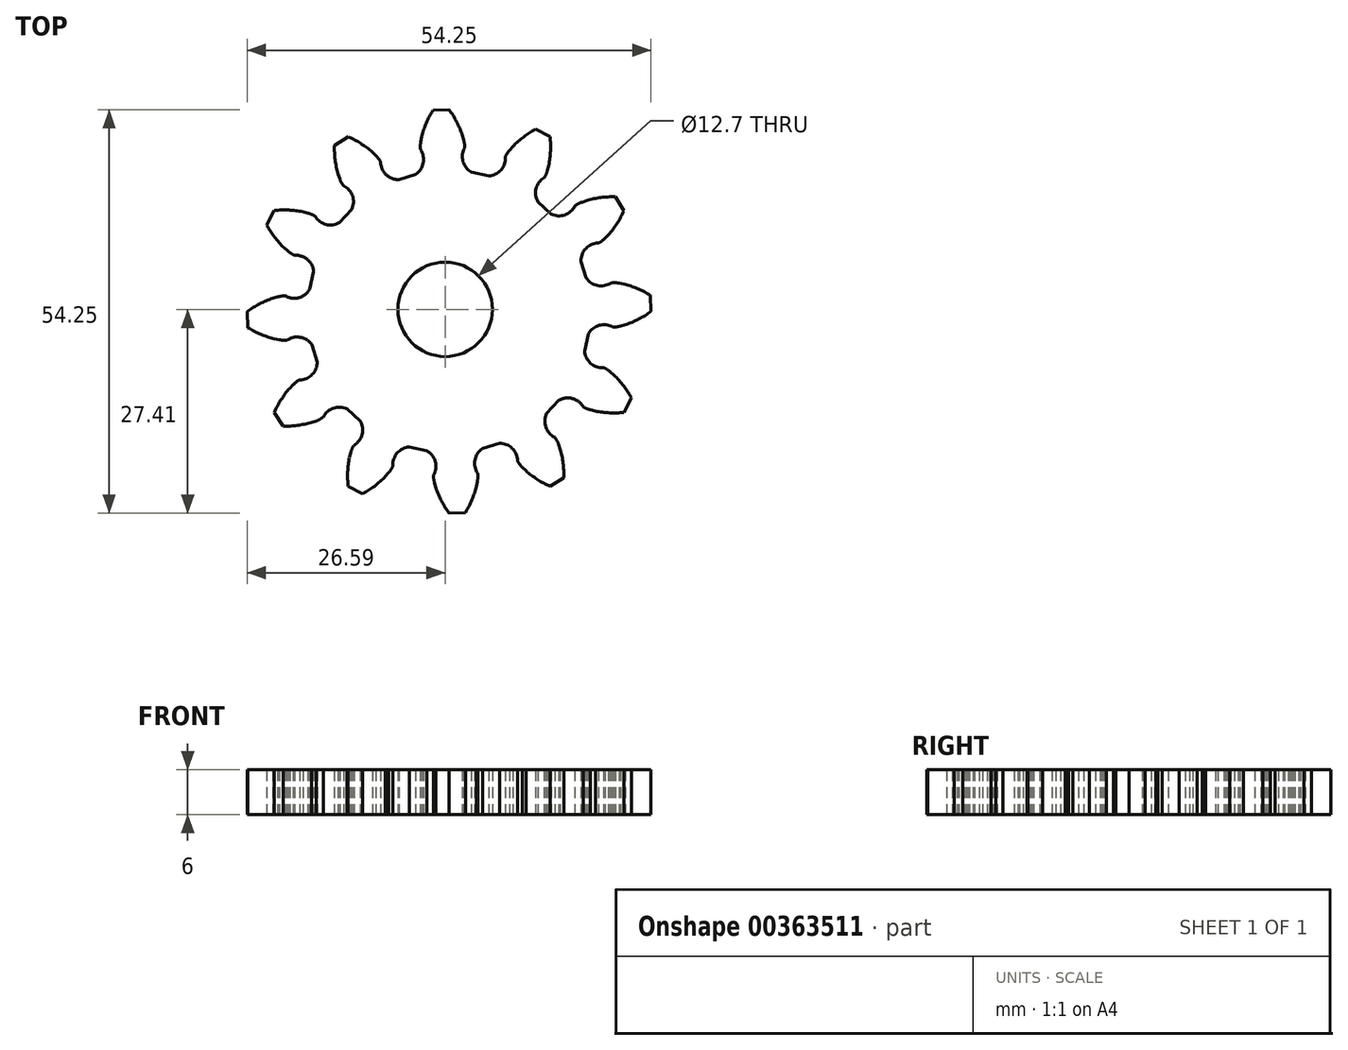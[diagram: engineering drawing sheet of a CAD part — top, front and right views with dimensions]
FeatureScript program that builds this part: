
annotation { "Feature Type Name" : "Feature", "Feature Type Description" : "" }
export const myFeature = defineFeature(function(context is Context, id is Id, definition is map)
    precondition{}
    {
        {
            var Q0;
            Q0=qCreatedBy(makeId("Top.planeOp"),FACE);
            var sketch = newSketch(context, id + "F0", { "sketchPlane" : qUnion([Q0])});
            skArc(sketch, "E0", {"start": v(-66.07, 34.96) * mm, "mid": v(-64.65, 34.9) * mm, "end": v(-63.23, 34.87) * mm});
            skCircle(sketch, "E1", {"center": v(0.54, -0.3) * mm, "radius": 3.17 * mm});
            skLineSegment(sketch, "E2", {"start": v(5.85, 17.92) * mm, "end": v(3.53, 18.44) * mm});
            skArc(sketch, "E3", {"start": v(2.6, 21.7) * mm, "mid": v(2.4, 19.87) * mm, "end": v(3.53, 18.44) * mm});
            skArc(sketch, "E4", {"start": v(2.6, 21.7) * mm, "mid": v(2.6, 22.24) * mm, "end": v(2.48, 22.77) * mm});
            skLineSegment(sketch, "E5", {"start": v(2.48, 22.77) * mm, "end": v(2.3, 23.42) * mm});
            skArc(sketch, "E6", {"start": v(2.3, 23.42) * mm, "mid": v(1.55, 25.2) * mm, "end": v(0.54, 26.84) * mm});
            skLineSegment(sketch, "E7", {"start": v(0.54, 26.84) * mm, "end": v(-1.65, 26.75) * mm});
            skArc(sketch, "E8", {"start": v(-1.65, 26.75) * mm, "mid": v(-2.53, 25.03) * mm, "end": v(-3.14, 23.2) * mm});
            skLineSegment(sketch, "E9", {"start": v(-3.14, 23.2) * mm, "end": v(-3.26, 22.54) * mm});
            skArc(sketch, "E10", {"start": v(-3.26, 22.54) * mm, "mid": v(-3.33, 22) * mm, "end": v(-3.3, 21.45) * mm});
            skArc(sketch, "E11", {"start": v(-3.96, 18.14) * mm, "mid": v(-2.94, 19.66) * mm, "end": v(-3.3, 21.45) * mm});
            skLineSegment(sketch, "E12", {"start": v(-3.96, 18.14) * mm, "end": v(-6.23, 17.43) * mm});
            skArc(sketch, "E13", {"start": v(-8.66, 19.78) * mm, "mid": v(-7.93, 18.1) * mm, "end": v(-6.23, 17.43) * mm});
            skArc(sketch, "E14", {"start": v(-8.66, 19.78) * mm, "mid": v(-8.94, 20.25) * mm, "end": v(-9.3, 20.66) * mm});
            skLineSegment(sketch, "E15", {"start": v(-9.3, 20.66) * mm, "end": v(-9.79, 21.13) * mm});
            skArc(sketch, "E16", {"start": v(-9.79, 21.13) * mm, "mid": v(-11.33, 22.3) * mm, "end": v(-13.02, 23.2) * mm});
            skLineSegment(sketch, "E17", {"start": v(-13.02, 23.2) * mm, "end": v(-14.88, 22.03) * mm});
            skArc(sketch, "E18", {"start": v(-14.88, 22.03) * mm, "mid": v(-14.78, 20.1) * mm, "end": v(-14.4, 18.22) * mm});
            skLineSegment(sketch, "E19", {"start": v(-14.4, 18.22) * mm, "end": v(-14.17, 17.58) * mm});
            skArc(sketch, "E20", {"start": v(-14.17, 17.58) * mm, "mid": v(-13.96, 17.08) * mm, "end": v(-13.66, 16.62) * mm});
            skArc(sketch, "E21", {"start": v(-12.57, 13.42) * mm, "mid": v(-12.45, 15.25) * mm, "end": v(-13.66, 16.62) * mm});
            skLineSegment(sketch, "E22", {"start": v(-12.57, 13.42) * mm, "end": v(-14.18, 11.67) * mm});
            skArc(sketch, "E23", {"start": v(-17.47, 12.5) * mm, "mid": v(-16, 11.4) * mm, "end": v(-14.18, 11.67) * mm});
            skArc(sketch, "E24", {"start": v(-17.47, 12.5) * mm, "mid": v(-17.94, 12.76) * mm, "end": v(-18.46, 12.93) * mm});
            skLineSegment(sketch, "E25", {"start": v(-18.46, 12.93) * mm, "end": v(-19.11, 13.1) * mm});
            skArc(sketch, "E26", {"start": v(-19.11, 13.1) * mm, "mid": v(-21.03, 13.34) * mm, "end": v(-22.95, 13.28) * mm});
            skLineSegment(sketch, "E27", {"start": v(-22.95, 13.28) * mm, "end": v(-23.97, 11.34) * mm});
            skArc(sketch, "E28", {"start": v(-23.97, 11.34) * mm, "mid": v(-22.93, 9.72) * mm, "end": v(-21.65, 8.28) * mm});
            skLineSegment(sketch, "E29", {"start": v(-21.65, 8.28) * mm, "end": v(-21.13, 7.84) * mm});
            skArc(sketch, "E30", {"start": v(-21.13, 7.84) * mm, "mid": v(-20.7, 7.5) * mm, "end": v(-20.21, 7.26) * mm});
            skArc(sketch, "E31", {"start": v(-17.67, 5.03) * mm, "mid": v(-18.48, 6.67) * mm, "end": v(-20.21, 7.26) * mm});
            skLineSegment(sketch, "E32", {"start": v(-17.67, 5.03) * mm, "end": v(-18.2, 2.71) * mm});
            skArc(sketch, "E33", {"start": v(-21.45, 1.78) * mm, "mid": v(-19.63, 1.57) * mm, "end": v(-18.2, 2.71) * mm});
            skArc(sketch, "E34", {"start": v(-21.45, 1.78) * mm, "mid": v(-22, 1.77) * mm, "end": v(-22.53, 1.66) * mm});
            skLineSegment(sketch, "E35", {"start": v(-22.53, 1.66) * mm, "end": v(-23.18, 1.48) * mm});
            skArc(sketch, "E36", {"start": v(-23.18, 1.48) * mm, "mid": v(-24.95, 0.73) * mm, "end": v(-26.6, -0.28) * mm});
            skLineSegment(sketch, "E37", {"start": v(-26.6, -0.28) * mm, "end": v(-26.5, -2.48) * mm});
            skArc(sketch, "E38", {"start": v(-26.5, -2.48) * mm, "mid": v(-24.79, -3.36) * mm, "end": v(-22.96, -3.96) * mm});
            skLineSegment(sketch, "E39", {"start": v(-22.96, -3.96) * mm, "end": v(-22.3, -4.08) * mm});
            skArc(sketch, "E40", {"start": v(-22.3, -4.08) * mm, "mid": v(-21.75, -4.16) * mm, "end": v(-21.2, -4.12) * mm});
            skArc(sketch, "E41", {"start": v(-17.89, -4.78) * mm, "mid": v(-19.41, -3.77) * mm, "end": v(-21.2, -4.12) * mm});
            skLineSegment(sketch, "E42", {"start": v(-17.89, -4.78) * mm, "end": v(-17.18, -7.05) * mm});
            skArc(sketch, "E43", {"start": v(-19.54, -9.48) * mm, "mid": v(-17.86, -8.76) * mm, "end": v(-17.18, -7.05) * mm});
            skArc(sketch, "E44", {"start": v(-19.54, -9.48) * mm, "mid": v(-20, -9.77) * mm, "end": v(-20.4, -10.13) * mm});
            skLineSegment(sketch, "E45", {"start": v(-20.4, -10.13) * mm, "end": v(-20.88, -10.61) * mm});
            skArc(sketch, "E46", {"start": v(-20.88, -10.61) * mm, "mid": v(-22.05, -12.15) * mm, "end": v(-22.96, -13.85) * mm});
            skLineSegment(sketch, "E47", {"start": v(-22.96, -13.85) * mm, "end": v(-21.79, -15.7) * mm});
            skArc(sketch, "E48", {"start": v(-21.79, -15.7) * mm, "mid": v(-19.86, -15.6) * mm, "end": v(-17.97, -15.21) * mm});
            skLineSegment(sketch, "E49", {"start": v(-17.97, -15.21) * mm, "end": v(-17.34, -15) * mm});
            skArc(sketch, "E50", {"start": v(-17.34, -15) * mm, "mid": v(-16.83, -14.78) * mm, "end": v(-16.38, -14.48) * mm});
            skArc(sketch, "E51", {"start": v(-13.17, -13.4) * mm, "mid": v(-15, -13.27) * mm, "end": v(-16.38, -14.48) * mm});
            skLineSegment(sketch, "E52", {"start": v(-13.17, -13.4) * mm, "end": v(-11.43, -15) * mm});
            skArc(sketch, "E53", {"start": v(-12.25, -18.29) * mm, "mid": v(-11.16, -16.82) * mm, "end": v(-11.43, -15) * mm});
            skArc(sketch, "E54", {"start": v(-12.25, -18.29) * mm, "mid": v(-12.51, -18.77) * mm, "end": v(-12.68, -19.29) * mm});
            skLineSegment(sketch, "E55", {"start": v(-12.68, -19.29) * mm, "end": v(-12.85, -19.94) * mm});
            skArc(sketch, "E56", {"start": v(-12.85, -19.94) * mm, "mid": v(-13.1, -21.85) * mm, "end": v(-13.03, -23.78) * mm});
            skLineSegment(sketch, "E57", {"start": v(-13.03, -23.78) * mm, "end": v(-11.1, -24.8) * mm});
            skArc(sketch, "E58", {"start": v(-11.1, -24.8) * mm, "mid": v(-9.47, -23.75) * mm, "end": v(-8.03, -22.47) * mm});
            skLineSegment(sketch, "E59", {"start": v(-8.03, -22.47) * mm, "end": v(-7.6, -21.96) * mm});
            skArc(sketch, "E60", {"start": v(-7.6, -21.96) * mm, "mid": v(-7.26, -21.52) * mm, "end": v(-7.02, -21.04) * mm});
            skArc(sketch, "E61", {"start": v(-4.78, -18.5) * mm, "mid": v(-6.43, -19.3) * mm, "end": v(-7.02, -21.04) * mm});
            skLineSegment(sketch, "E62", {"start": v(-4.78, -18.5) * mm, "end": v(-2.46, -19.01) * mm});
            skArc(sketch, "E63", {"start": v(-1.54, -22.27) * mm, "mid": v(-1.33, -20.45) * mm, "end": v(-2.46, -19.01) * mm});
            skArc(sketch, "E64", {"start": v(-1.54, -22.27) * mm, "mid": v(-1.53, -22.81) * mm, "end": v(-1.41, -23.35) * mm});
            skLineSegment(sketch, "E65", {"start": v(-1.41, -23.35) * mm, "end": v(-1.24, -24) * mm});
            skArc(sketch, "E66", {"start": v(-1.24, -24) * mm, "mid": v(-0.49, -25.77) * mm, "end": v(0.53, -27.41) * mm});
            skLineSegment(sketch, "E67", {"start": v(0.53, -27.41) * mm, "end": v(2.72, -27.32) * mm});
            skArc(sketch, "E68", {"start": v(2.72, -27.32) * mm, "mid": v(3.6, -25.6) * mm, "end": v(4.2, -23.78) * mm});
            skLineSegment(sketch, "E69", {"start": v(4.2, -23.78) * mm, "end": v(4.33, -23.12) * mm});
            skArc(sketch, "E70", {"start": v(4.33, -23.12) * mm, "mid": v(4.4, -22.58) * mm, "end": v(4.37, -22.03) * mm});
            skArc(sketch, "E71", {"start": v(5.03, -18.71) * mm, "mid": v(4.01, -20.23) * mm, "end": v(4.37, -22.03) * mm});
            skLineSegment(sketch, "E72", {"start": v(5.03, -18.71) * mm, "end": v(7.3, -18) * mm});
            skArc(sketch, "E73", {"start": v(9.73, -20.36) * mm, "mid": v(9, -18.68) * mm, "end": v(7.3, -18) * mm});
            skArc(sketch, "E74", {"start": v(9.73, -20.36) * mm, "mid": v(10.01, -20.83) * mm, "end": v(10.38, -21.23) * mm});
            skLineSegment(sketch, "E75", {"start": v(10.38, -21.23) * mm, "end": v(10.86, -21.7) * mm});
            skArc(sketch, "E76", {"start": v(10.86, -21.7) * mm, "mid": v(12.4, -22.87) * mm, "end": v(14.1, -23.78) * mm});
            skLineSegment(sketch, "E77", {"start": v(14.1, -23.78) * mm, "end": v(15.95, -22.6) * mm});
            skArc(sketch, "E78", {"start": v(15.95, -22.6) * mm, "mid": v(15.85, -20.68) * mm, "end": v(15.46, -18.8) * mm});
            skLineSegment(sketch, "E79", {"start": v(15.46, -18.8) * mm, "end": v(15.24, -18.16) * mm});
            skArc(sketch, "E80", {"start": v(15.24, -18.16) * mm, "mid": v(15.03, -17.66) * mm, "end": v(14.73, -17.2) * mm});
            skArc(sketch, "E81", {"start": v(13.64, -14) * mm, "mid": v(13.52, -15.82) * mm, "end": v(14.73, -17.2) * mm});
            skLineSegment(sketch, "E82", {"start": v(13.64, -14) * mm, "end": v(15.25, -12.25) * mm});
            skArc(sketch, "E83", {"start": v(18.53, -13.07) * mm, "mid": v(17.06, -11.98) * mm, "end": v(15.25, -12.25) * mm});
            skArc(sketch, "E84", {"start": v(18.53, -13.07) * mm, "mid": v(19.01, -13.34) * mm, "end": v(19.53, -13.5) * mm});
            skLineSegment(sketch, "E85", {"start": v(19.53, -13.5) * mm, "end": v(20.18, -13.68) * mm});
            skArc(sketch, "E86", {"start": v(20.18, -13.68) * mm, "mid": v(22.1, -13.91) * mm, "end": v(24.02, -13.85) * mm});
            skLineSegment(sketch, "E87", {"start": v(24.02, -13.85) * mm, "end": v(25.04, -11.91) * mm});
            skArc(sketch, "E88", {"start": v(25.04, -11.91) * mm, "mid": v(24, -10.3) * mm, "end": v(22.71, -8.85) * mm});
            skLineSegment(sketch, "E89", {"start": v(22.71, -8.85) * mm, "end": v(22.2, -8.42) * mm});
            skArc(sketch, "E90", {"start": v(22.2, -8.42) * mm, "mid": v(21.77, -8.08) * mm, "end": v(21.28, -7.84) * mm});
            skArc(sketch, "E91", {"start": v(18.74, -5.6) * mm, "mid": v(19.55, -7.25) * mm, "end": v(21.28, -7.84) * mm});
            skLineSegment(sketch, "E92", {"start": v(18.74, -5.6) * mm, "end": v(19.26, -3.29) * mm});
            skArc(sketch, "E93", {"start": v(22.52, -2.36) * mm, "mid": v(20.7, -2.15) * mm, "end": v(19.26, -3.29) * mm});
            skArc(sketch, "E94", {"start": v(22.52, -2.36) * mm, "mid": v(23.06, -2.35) * mm, "end": v(23.6, -2.24) * mm});
            skLineSegment(sketch, "E95", {"start": v(23.6, -2.24) * mm, "end": v(24.24, -2.06) * mm});
            skArc(sketch, "E96", {"start": v(24.24, -2.06) * mm, "mid": v(26.02, -1.3) * mm, "end": v(27.66, -0.3) * mm});
            skLineSegment(sketch, "E97", {"start": v(27.66, -0.3) * mm, "end": v(27.57, 1.9) * mm});
            skArc(sketch, "E98", {"start": v(27.57, 1.9) * mm, "mid": v(25.86, 2.78) * mm, "end": v(24.03, 3.38) * mm});
            skLineSegment(sketch, "E99", {"start": v(24.03, 3.38) * mm, "end": v(23.36, 3.5) * mm});
            skArc(sketch, "E100", {"start": v(23.36, 3.5) * mm, "mid": v(22.82, 3.58) * mm, "end": v(22.28, 3.55) * mm});
            skArc(sketch, "E101", {"start": v(18.96, 4.2) * mm, "mid": v(20.48, 3.19) * mm, "end": v(22.28, 3.55) * mm});
            skLineSegment(sketch, "E102", {"start": v(18.96, 4.2) * mm, "end": v(18.25, 6.48) * mm});
            skArc(sketch, "E103", {"start": v(20.6, 8.9) * mm, "mid": v(18.93, 8.18) * mm, "end": v(18.25, 6.48) * mm});
            skArc(sketch, "E104", {"start": v(20.6, 8.9) * mm, "mid": v(21.07, 9.19) * mm, "end": v(21.48, 9.56) * mm});
            skLineSegment(sketch, "E105", {"start": v(21.48, 9.56) * mm, "end": v(21.95, 10.03) * mm});
            skArc(sketch, "E106", {"start": v(21.95, 10.03) * mm, "mid": v(23.12, 11.57) * mm, "end": v(24.03, 13.27) * mm});
            skLineSegment(sketch, "E107", {"start": v(24.03, 13.27) * mm, "end": v(22.86, 15.12) * mm});
            skArc(sketch, "E108", {"start": v(22.86, 15.12) * mm, "mid": v(20.93, 15.03) * mm, "end": v(19.04, 14.64) * mm});
            skLineSegment(sketch, "E109", {"start": v(19.04, 14.64) * mm, "end": v(18.4, 14.41) * mm});
            skArc(sketch, "E110", {"start": v(18.4, 14.41) * mm, "mid": v(17.9, 14.2) * mm, "end": v(17.45, 13.9) * mm});
            skArc(sketch, "E111", {"start": v(14.24, 12.82) * mm, "mid": v(16.07, 12.7) * mm, "end": v(17.45, 13.9) * mm});
            skLineSegment(sketch, "E112", {"start": v(14.24, 12.82) * mm, "end": v(12.5, 14.43) * mm});
            skArc(sketch, "E113", {"start": v(13.32, 17.71) * mm, "mid": v(12.23, 16.24) * mm, "end": v(12.5, 14.43) * mm});
            skArc(sketch, "E114", {"start": v(13.32, 17.71) * mm, "mid": v(13.58, 18.19) * mm, "end": v(13.75, 18.7) * mm});
            skLineSegment(sketch, "E115", {"start": v(13.75, 18.7) * mm, "end": v(13.92, 19.36) * mm});
            skArc(sketch, "E116", {"start": v(13.92, 19.36) * mm, "mid": v(14.16, 21.27) * mm, "end": v(14.1, 23.2) * mm});
            skLineSegment(sketch, "E117", {"start": v(14.1, 23.2) * mm, "end": v(12.16, 24.22) * mm});
            skArc(sketch, "E118", {"start": v(12.16, 24.22) * mm, "mid": v(10.54, 23.17) * mm, "end": v(9.1, 21.9) * mm});
            skLineSegment(sketch, "E119", {"start": v(9.1, 21.9) * mm, "end": v(8.66, 21.38) * mm});
            skArc(sketch, "E120", {"start": v(8.66, 21.38) * mm, "mid": v(8.33, 20.95) * mm, "end": v(8.09, 20.46) * mm});
            skArc(sketch, "E121", {"start": v(5.85, 17.92) * mm, "mid": v(7.5, 18.72) * mm, "end": v(8.09, 20.46) * mm});
            skSolve(sketch);
        }
        {
            var Q0;
            Q0 = qSketchRegion(id + "F0", true);
            extrude(context, id + "F1", {"entities" : qUnion([Q0]), "depth" : 6 * mm});
        }
        {
            var Q0;
            Q0=qCreatedBy(makeId("Top.planeOp"),FACE);
            var sketch = newSketch(context, id + "F2", { "sketchPlane" : qUnion([Q0])});
            skCircle(sketch, "E122", {"center": v(0, 0) * mm, "radius": 6.35 * mm});
            skSolve(sketch);
        }
        {
            var Q0;
            Q0=makeQuery(id+"F2.imprint","IMPRINT",FACE,{"disambiguationData":[TD([[makeQuery(id+"F2.imprint","IMPRINT",EDGE,{"derivedFrom":sQuery(id+"F2.wireOp",EDGE,"E122")}),1.0]])]});
            extrude(context, id + "F3", {"entities" : qUnion([Q0]), "operationType" : NewBodyOperationType.REMOVE, "depth" : 6 * mm});
        }
    });
